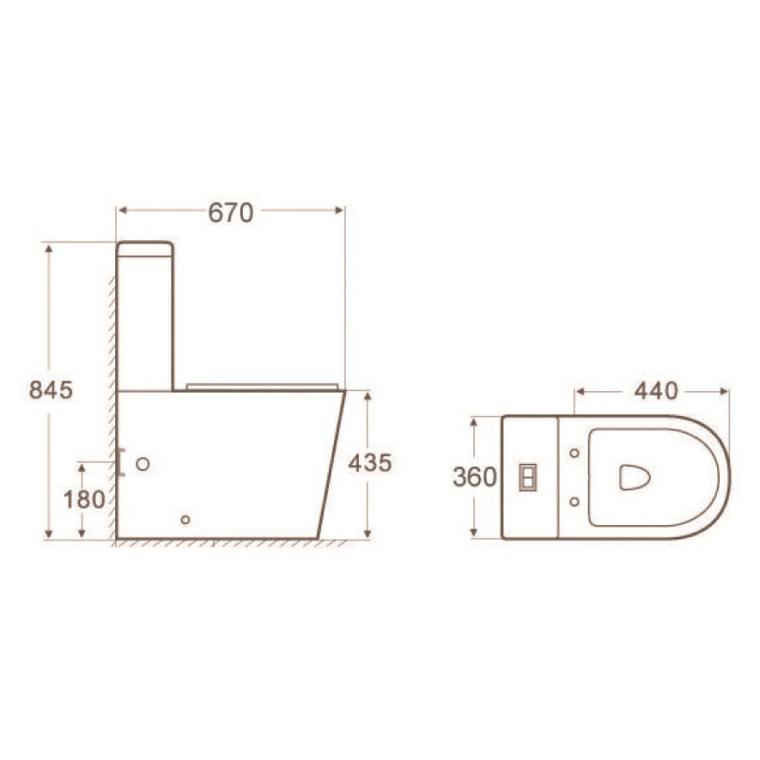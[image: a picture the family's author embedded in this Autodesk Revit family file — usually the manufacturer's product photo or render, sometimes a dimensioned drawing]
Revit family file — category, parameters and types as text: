
# Revit family: LIXIL - 439550WH - VAAL ORCHID TOILET PAN WALL HUNG
name_source: partatom
category: Plumbing Fixtures
units: mm (PartAtom-declared; Revit-internal decimal feet)

## family parameters
Always vertical = Yes
Cut with Voids When Loaded = No
Enable Cutting in Views = No
Maintain Annotation Orientation = No
OmniClass Number = 23.45.00.00
OmniClass Title = Sanitary, Laundry, and Cleaning Equipment
Part Type = Normal
Room Calculation Point = No
Round Connector Dimension = Use Diameter
Shared = Yes
Work Plane-Based = No

## types (1)
- 439550WH
    CW Connection Diameter = 55 mm  [stored 0.180446 ft]
    CW Connection Radius = 28 mm
    Default Elevation = 0 mm  [stored 0 ft]
    Description = Vaal Orchid toilet pan to detail and spec. See sanware schedule. Available from Lixil.
    Hosted on lixil.co.za = https://www.lixil.co.za
    M _ CISTERN = M _ LIXIL - VAAL - PORCELAIN - WHITE 01
    M _ WC = M _ LIXIL - VAAL - PORCELAIN - WHITE 01
    M _ WC LID AND SEAT = M _ LIXIL - VAAL - PLASTIC - WHITE 01
    M _ WC SEAT SS FITTINGS = M _ LIXIL - STAINLESS STEEL 01
    M _ WC SEAT SUPPORT = M _ LIXIL - VAAL - PLASTIC - WHITE 01
    Product Specification = Supplier: Lixil.
Product description: Back inlet closed rim pan. Compatible with concealed cistern, duct cistern or concealed flush valve. Designed to flush effectively on 6/3L.
10 Year Warranty Cobra Genuine 
Product Code: CORBCCNN-2CO0413.
SKU Code	: 439550WH.
Barcode: 6005826067026.
Brand: Vaal.
Range: Orchid.
Category: Toilets.
Sub-Category: Pans.
Material: Ceramic.
Colour: White.
Package Height: 400 mm
Package Width: 370 mm
Package Length: 570 mm
Product Height: 410mm
Product Width: 392 mm
Product Length: 556 mm
Package Volume: 84360000 mm³
Package Weight: 15.4 kg

Notes:
- Refer to manufacturer's and supplier's installation, maintenance and cleaning manual.
- Refer to manufacturer's and supplier's guarantees and warrantees document.
    Waste Connection Diameter = 102 mm
    Waste Connection Radius = 51 mm

note: [stored X ft] marks values corroborated as IEEE doubles in the binary element streams (Revit-internal decimal feet)

## geometry (parser evidence)
native form markers: Sweep x27
no freeform markers — native parametric forms only
